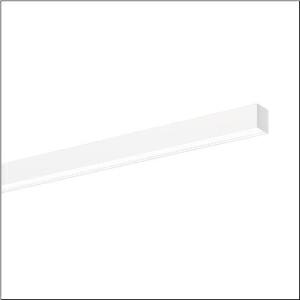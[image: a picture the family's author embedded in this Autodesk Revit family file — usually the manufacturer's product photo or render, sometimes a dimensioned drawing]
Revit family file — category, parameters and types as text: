
# Revit family: silica_r__21_51mx23dc4awb_8ea6
name_source: partatom
category: Lighting Fixtures
units: mm (PartAtom-declared; Revit-internal decimal feet)

## family parameters
Cut with Voids When Loaded = No
Host = Face
Light Source = No
Part Type = Normal
Room Calculation Point = No
Round Connector Dimension = Use Diameter
Shared = No

## types (1)
- --- (1 x LED, 8200 lm, 58.2 W, 4000K)
    Apparent Load = 58 VA
    CIE Flux Codes = 78 96 99 100 100
    Color Rendering = 80
    Color Temperature = 4000K
    Default Elevation = 1800 mm
    Description = Silica® 21, office luminaire, primary optical cover: prismatic diffuser, of PMMA, CAT 2 (L<= 3000cd/m²), light emission: direct distribution, primary light characteristic: symmetric, installation type: surface-mounted, LED, rated luminous flux: 8.200lm, luminous efficacy: 141lm/W, light colour: 840, colour temperature: 4000K, with terminal, 3+2-pole, max. 2.5mm², mains connection: 220..240V, AC, 50/60Hz, rated input power: 58.2W, luminaire housing, of aluminium, traffic white (RAL 9016), length: 3.004mm, width: 53mm, height: 53mm, protection rating (complete): IP20, insulation class (complete): insulation class I (protective earthing), certification: CE, permissible operating ambient temperature: 0..+35°C, standard: EN 50419, packaging unit: 1 piece
    Height = 0 mm  [stored 0 ft]
    Lamp = 1 x LED
    Lamp Light Flux = 8200 lm
    Lamp Power = 58.2 W
    Lamp count = 1
    Length = 3004 mm
    Luminous efficacy = 141 lm/W
    Manufacturer = Siteco
    ModVariant = No
    Model = 51MX23DC4AWB
    Mounting Place = Ceiling
    Mounting Type = Recessed
    Number of Poles = 1
    OnlyDefault = Yes
    Power Factor = 1
    Product Name = Silica® 21
    Product group = office luminaire | ceiling recessed
    ProductGroupID = 401
    Protection Class = Protection class I
    Protection Degree = IP 20
    RLX_Detail_Level = 1
    RLX_Emergency_Light_Flux = 0 lm
    RLX_Emergency_Type = 0
    RLX_Emergency_Type_DB = No
    RlxData = <blob elided: 18609 chars, md5=dc5337b3>
    Socket = socket
    Standby Power = 0 W
    System Light Flux = 8200 lm
    System Power = 58 W
    Type Comments = factory setting: luminous flux: 100 % | dim-lin: 254 | 323 mA
    Type Image = l_1297777.jpg
    URL = http://relux.com
    VarID = @adj_050117
    Voltage = 0 V
    Weight = 0.00 kg
    Width = 53 mm

note: [stored X ft] marks values corroborated as IEEE doubles in the binary element streams (Revit-internal decimal feet)

## geometry (parser evidence)
native form markers: Blend x4, Sweep x9
no freeform markers — native parametric forms only
